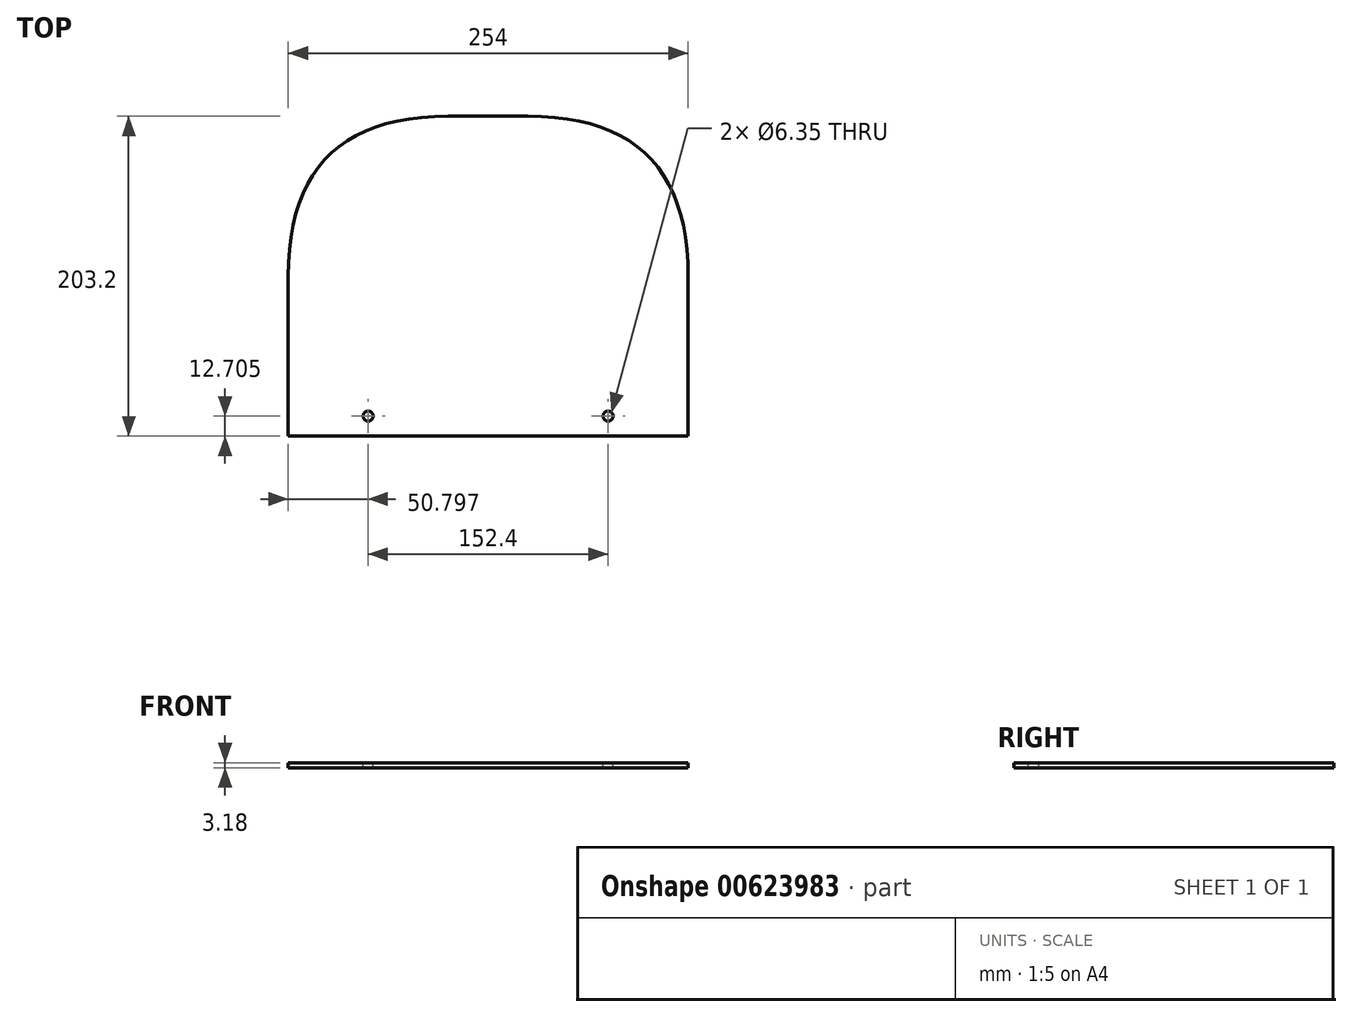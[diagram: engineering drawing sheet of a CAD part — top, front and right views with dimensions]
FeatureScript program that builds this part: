
annotation { "Feature Type Name" : "Feature", "Feature Type Description" : "" }
export const myFeature = defineFeature(function(context is Context, id is Id, definition is map)
    precondition{}
    {
        {
            var Q0;
            Q0=qCreatedBy(makeId("Top.planeOp"),FACE);
            var sketch = newSketch(context, id + "F0", { "sketchPlane" : qUnion([Q0])});
            skLineSegment(sketch, "E0.bottom", {"start": v(-136.18, -89.9) * mm, "end": v(117.82, -89.9) * mm});
            skLineSegment(sketch, "E0.top", {"start": v(-136.18, 113.3) * mm, "end": v(117.82, 113.3) * mm});
            skLineSegment(sketch, "E0.left", {"start": v(-136.18, -89.9) * mm, "end": v(-136.18, 113.3) * mm});
            skLineSegment(sketch, "E0.right", {"start": v(117.82, -89.9) * mm, "end": v(117.82, 113.3) * mm});
            skSolve(sketch);
        }
        {
            var Q0;
            Q0=makeQuery(id+"F0.imprint","IMPRINT",FACE,{"disambiguationData":[TD([[makeQuery(id+"F0.imprint","IMPRINT",EDGE,{"derivedFrom":sQuery(id+"F0.wireOp",EDGE,"E0.bottom")}),1.0]])]});
            extrude(context, id + "F1", {"entities" : qUnion([Q0]), "depth" : 3.17 * mm, "offsetDistance" : 25.4 * mm});
        }
        {
            var Q0;
            Q0=makeQuery(id+"F1.opExtrude","SWEPT_EDGE",EDGE,{"disambiguationData":[OSD([sQuery(id+"F0.wireOp",EDGE,"E0.top"),sQuery(id+"F0.wireOp",EDGE,"E0.left")])]});
            var Q1;
            Q1=makeQuery(id+"F1.opExtrude","SWEPT_EDGE",EDGE,{"disambiguationData":[OSD([sQuery(id+"F0.wireOp",EDGE,"E0.top"),sQuery(id+"F0.wireOp",EDGE,"E0.right")])]});
            fillet(context, id + "F2", {"entities" : qUnion([Q0, Q1]), "radius" : 101.6 * mm, "tangentPropagation" : true, "rho" : 0.5, "crossSection" : FilletCrossSection.CONIC, "allowEdgeOverflow" : false});
        }
        {
            var Q0;
            Q0=makeQuery(id+"F1.opExtrude","CAP_FACE",FACE,{"disambiguationData":[OSD([sQuery(id+"F0.wireOp",EDGE,"E0.bottom"),sQuery(id+"F0.wireOp",EDGE,"E0.top"),sQuery(id+"F0.wireOp",EDGE,"E0.left"),sQuery(id+"F0.wireOp",EDGE,"E0.right")])],"isStart":false});
            var sketch = newSketch(context, id + "F3", { "sketchPlane" : qUnion([Q0])});
            skCircle(sketch, "E1", {"center": v(-85.38, -77.2) * mm, "radius": 3.18 * mm});
            skCircle(sketch, "E2", {"center": v(67.02, -77.2) * mm, "radius": 3.18 * mm});
            skSolve(sketch);
        }
        {
            var Q0;
            Q0=makeQuery(id+"F3.imprint","IMPRINT",FACE,{"disambiguationData":[TD([[makeQuery(id+"F3.imprint","IMPRINT",EDGE,{"derivedFrom":sQuery(id+"F3.wireOp",EDGE,"E1")}),1.0]])]});
            var Q1;
            Q1=makeQuery(id+"F3.imprint","IMPRINT",FACE,{"disambiguationData":[TD([[makeQuery(id+"F3.imprint","IMPRINT",EDGE,{"derivedFrom":sQuery(id+"F3.wireOp",EDGE,"E2")}),1.0]])]});
            extrude(context, id + "F4", {"entities" : qUnion([Q0, Q1]), "operationType" : NewBodyOperationType.REMOVE, "oppositeDirection" : true, "depth" : 3.17 * mm, "offsetDistance" : 25.4 * mm});
        }
    });
